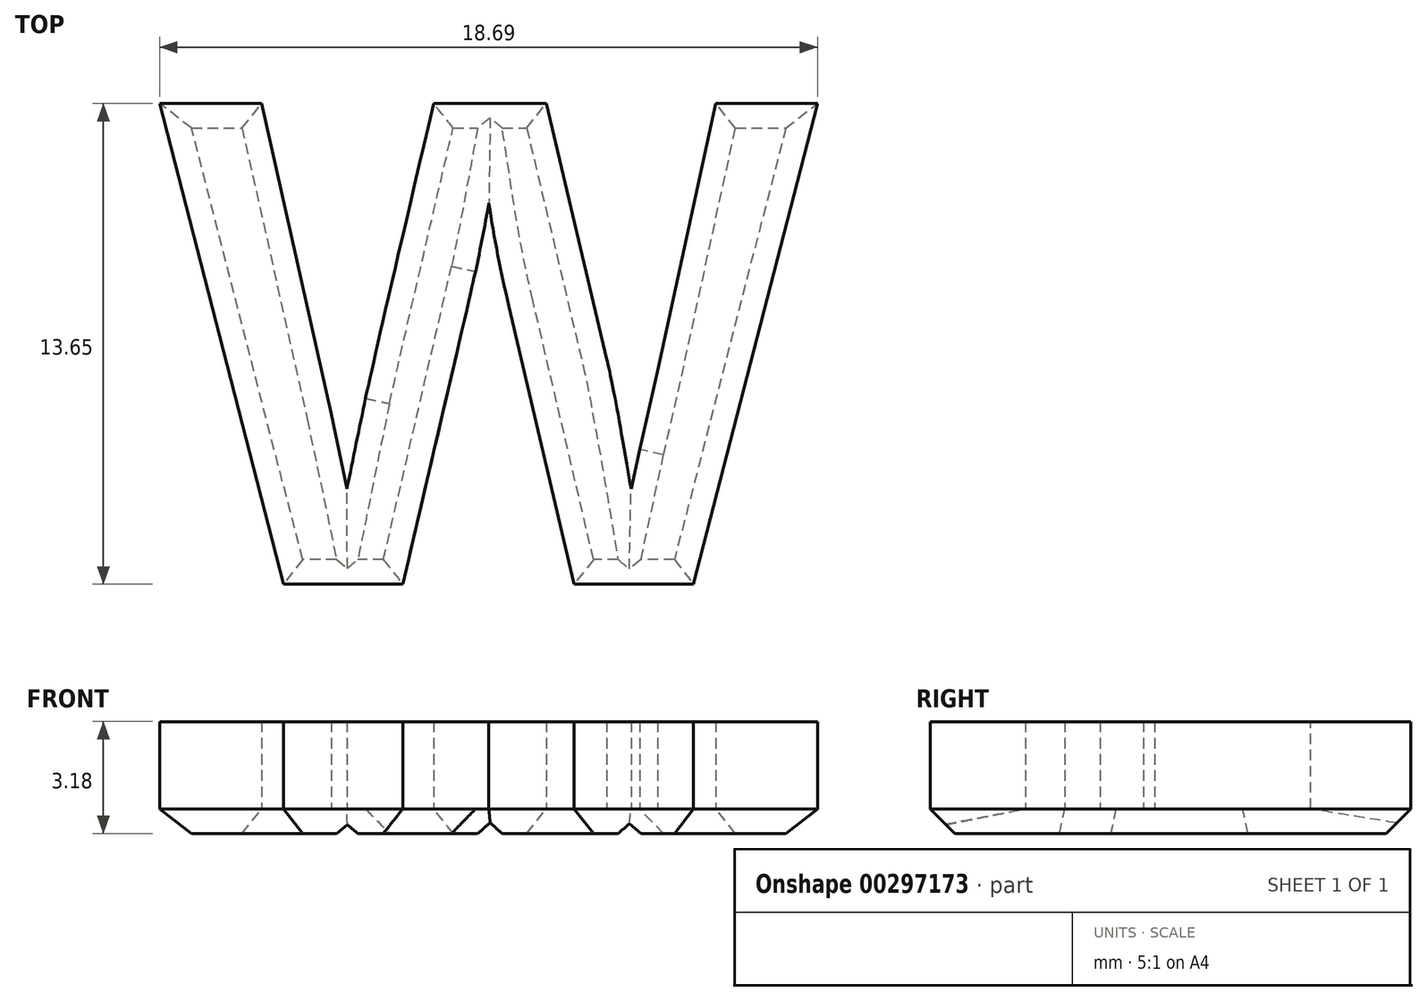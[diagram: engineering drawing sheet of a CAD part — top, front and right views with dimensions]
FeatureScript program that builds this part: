
annotation { "Feature Type Name" : "Feature", "Feature Type Description" : "" }
export const myFeature = defineFeature(function(context is Context, id is Id, definition is map)
    precondition{}
    {
        {
            var Q0;
            Q0=qCreatedBy(makeId("Top.planeOp"),FACE);
            var sketch = newSketch(context, id + "F0", { "sketchPlane" : qUnion([Q0])});
            skText(sketch, "E0", { "text": "W", "fontName": "Arimo-Bold.ttf"});
            const initialGuessF0  = {"E0": [0, -0.01429, 1, 0, 0.01429]};
            skSetInitialGuess(sketch, initialGuessF0);
            skSolve(sketch);
        }
        {
            var Q0;
            Q0=qSketchRegion(id+"F0",true);
            var Q1;
            Q1=qSketchRegion(id+"FFuAMvX4B0CXexs_0",true);
            var Q2;
            Q2=qSketchRegion(id+"F3e2CQsKu9PIjX0_0",true);
            var Q3;
            Q3=qSketchRegion(id+"F9LWrLlmn86MAX7_0",true);
            extrude(context, id + "F1", {"entities" : qUnion([Q0, Q1, Q2, Q3]), "depth" : 3.17 * mm});
        }
        {
            var Q0;
            Q0=makeQuery(id+"F1.opExtrude","CAP_FACE",FACE,{"disambiguationData":[OSD([sQuery(id+"F3e2CQsKu9PIjX0_0.wireOp",EDGE,"d36403c4-1396-490d-9497-49aafdbeb43d.sketch_text.stroke-0"),sQuery(id+"F3e2CQsKu9PIjX0_0.wireOp",EDGE,"d36403c4-1396-490d-9497-49aafdbeb43d.sketch_text.stroke-1"),sQuery(id+"F3e2CQsKu9PIjX0_0.wireOp",EDGE,"d36403c4-1396-490d-9497-49aafdbeb43d.sketch_text.stroke-2"),sQuery(id+"F3e2CQsKu9PIjX0_0.wireOp",EDGE,"d36403c4-1396-490d-9497-49aafdbeb43d.sketch_text.stroke-3"),sQuery(id+"F3e2CQsKu9PIjX0_0.wireOp",EDGE,"d36403c4-1396-490d-9497-49aafdbeb43d.sketch_text.stroke-4"),sQuery(id+"F3e2CQsKu9PIjX0_0.wireOp",EDGE,"d36403c4-1396-490d-9497-49aafdbeb43d.sketch_text.stroke-5"),sQuery(id+"F3e2CQsKu9PIjX0_0.wireOp",EDGE,"d36403c4-1396-490d-9497-49aafdbeb43d.sketch_text.stroke-6"),sQuery(id+"F3e2CQsKu9PIjX0_0.wireOp",EDGE,"d36403c4-1396-490d-9497-49aafdbeb43d.sketch_text.stroke-7"),sQuery(id+"F3e2CQsKu9PIjX0_0.wireOp",EDGE,"d36403c4-1396-490d-9497-49aafdbeb43d.sketch_text.stroke-8"),sQuery(id+"F3e2CQsKu9PIjX0_0.wireOp",EDGE,"d36403c4-1396-490d-9497-49aafdbeb43d.sketch_text.stroke-9"),sQuery(id+"F3e2CQsKu9PIjX0_0.wireOp",EDGE,"d36403c4-1396-490d-9497-49aafdbeb43d.sketch_text.stroke-10"),sQuery(id+"F3e2CQsKu9PIjX0_0.wireOp",EDGE,"d36403c4-1396-490d-9497-49aafdbeb43d.sketch_text.stroke-11"),sQuery(id+"F3e2CQsKu9PIjX0_0.wireOp",EDGE,"d36403c4-1396-490d-9497-49aafdbeb43d.sketch_text.stroke-12"),sQuery(id+"F3e2CQsKu9PIjX0_0.wireOp",EDGE,"d36403c4-1396-490d-9497-49aafdbeb43d.sketch_text.stroke-13"),sQuery(id+"F3e2CQsKu9PIjX0_0.wireOp",EDGE,"d36403c4-1396-490d-9497-49aafdbeb43d.sketch_text.stroke-14"),sQuery(id+"F3e2CQsKu9PIjX0_0.wireOp",EDGE,"d36403c4-1396-490d-9497-49aafdbeb43d.sketch_text.stroke-15"),sQuery(id+"F3e2CQsKu9PIjX0_0.wireOp",EDGE,"d36403c4-1396-490d-9497-49aafdbeb43d.sketch_text.stroke-16"),sQuery(id+"F3e2CQsKu9PIjX0_0.wireOp",EDGE,"d36403c4-1396-490d-9497-49aafdbeb43d.sketch_text.stroke-17"),sQuery(id+"F3e2CQsKu9PIjX0_0.wireOp",EDGE,"d36403c4-1396-490d-9497-49aafdbeb43d.sketch_text.stroke-18"),sQuery(id+"F3e2CQsKu9PIjX0_0.wireOp",EDGE,"d36403c4-1396-490d-9497-49aafdbeb43d.sketch_text.stroke-19"),sQuery(id+"F3e2CQsKu9PIjX0_0.wireOp",EDGE,"d36403c4-1396-490d-9497-49aafdbeb43d.sketch_text.stroke-20")])],"isStart":true});
            var Q1;
            Q1=makeQuery(id+"F1.opExtrude","CAP_FACE",FACE,{"disambiguationData":[OSD([sQuery(id+"FFuAMvX4B0CXexs_0.wireOp",EDGE,"ff5d8e69-f4ea-49cc-82ca-cbd897854416.sketch_text.stroke-0"),sQuery(id+"FFuAMvX4B0CXexs_0.wireOp",EDGE,"ff5d8e69-f4ea-49cc-82ca-cbd897854416.sketch_text.stroke-1"),sQuery(id+"FFuAMvX4B0CXexs_0.wireOp",EDGE,"ff5d8e69-f4ea-49cc-82ca-cbd897854416.sketch_text.stroke-2"),sQuery(id+"FFuAMvX4B0CXexs_0.wireOp",EDGE,"ff5d8e69-f4ea-49cc-82ca-cbd897854416.sketch_text.stroke-3"),sQuery(id+"FFuAMvX4B0CXexs_0.wireOp",EDGE,"ff5d8e69-f4ea-49cc-82ca-cbd897854416.sketch_text.stroke-4"),sQuery(id+"FFuAMvX4B0CXexs_0.wireOp",EDGE,"ff5d8e69-f4ea-49cc-82ca-cbd897854416.sketch_text.stroke-5"),sQuery(id+"FFuAMvX4B0CXexs_0.wireOp",EDGE,"ff5d8e69-f4ea-49cc-82ca-cbd897854416.sketch_text.stroke-6"),sQuery(id+"FFuAMvX4B0CXexs_0.wireOp",EDGE,"ff5d8e69-f4ea-49cc-82ca-cbd897854416.sketch_text.stroke-7"),sQuery(id+"FFuAMvX4B0CXexs_0.wireOp",EDGE,"ff5d8e69-f4ea-49cc-82ca-cbd897854416.sketch_text.stroke-8"),sQuery(id+"FFuAMvX4B0CXexs_0.wireOp",EDGE,"ff5d8e69-f4ea-49cc-82ca-cbd897854416.sketch_text.stroke-9"),sQuery(id+"FFuAMvX4B0CXexs_0.wireOp",EDGE,"ff5d8e69-f4ea-49cc-82ca-cbd897854416.sketch_text.stroke-10"),sQuery(id+"FFuAMvX4B0CXexs_0.wireOp",EDGE,"ff5d8e69-f4ea-49cc-82ca-cbd897854416.sketch_text.stroke-11"),sQuery(id+"FFuAMvX4B0CXexs_0.wireOp",EDGE,"ff5d8e69-f4ea-49cc-82ca-cbd897854416.sketch_text.stroke-12"),sQuery(id+"FFuAMvX4B0CXexs_0.wireOp",EDGE,"ff5d8e69-f4ea-49cc-82ca-cbd897854416.sketch_text.stroke-13"),sQuery(id+"FFuAMvX4B0CXexs_0.wireOp",EDGE,"ff5d8e69-f4ea-49cc-82ca-cbd897854416.sketch_text.stroke-14"),sQuery(id+"FFuAMvX4B0CXexs_0.wireOp",EDGE,"ff5d8e69-f4ea-49cc-82ca-cbd897854416.sketch_text.stroke-15"),sQuery(id+"FFuAMvX4B0CXexs_0.wireOp",EDGE,"ff5d8e69-f4ea-49cc-82ca-cbd897854416.sketch_text.stroke-16")])],"isStart":true});
            var Q2;
            Q2=makeQuery(id+"F1.opExtrude","CAP_FACE",FACE,{"disambiguationData":[OSD([sQuery(id+"F9LWrLlmn86MAX7_0.wireOp",EDGE,"c90eff37-dab6-43ec-bed2-d4ad99606f9c.sketch_text.stroke-0"),sQuery(id+"F9LWrLlmn86MAX7_0.wireOp",EDGE,"c90eff37-dab6-43ec-bed2-d4ad99606f9c.sketch_text.stroke-1"),sQuery(id+"F9LWrLlmn86MAX7_0.wireOp",EDGE,"c90eff37-dab6-43ec-bed2-d4ad99606f9c.sketch_text.stroke-2"),sQuery(id+"F9LWrLlmn86MAX7_0.wireOp",EDGE,"c90eff37-dab6-43ec-bed2-d4ad99606f9c.sketch_text.stroke-3"),sQuery(id+"F9LWrLlmn86MAX7_0.wireOp",EDGE,"c90eff37-dab6-43ec-bed2-d4ad99606f9c.sketch_text.stroke-4"),sQuery(id+"F9LWrLlmn86MAX7_0.wireOp",EDGE,"c90eff37-dab6-43ec-bed2-d4ad99606f9c.sketch_text.stroke-5"),sQuery(id+"F9LWrLlmn86MAX7_0.wireOp",EDGE,"c90eff37-dab6-43ec-bed2-d4ad99606f9c.sketch_text.stroke-6"),sQuery(id+"F9LWrLlmn86MAX7_0.wireOp",EDGE,"c90eff37-dab6-43ec-bed2-d4ad99606f9c.sketch_text.stroke-7"),sQuery(id+"F9LWrLlmn86MAX7_0.wireOp",EDGE,"c90eff37-dab6-43ec-bed2-d4ad99606f9c.sketch_text.stroke-8"),sQuery(id+"F9LWrLlmn86MAX7_0.wireOp",EDGE,"c90eff37-dab6-43ec-bed2-d4ad99606f9c.sketch_text.stroke-9"),sQuery(id+"F9LWrLlmn86MAX7_0.wireOp",EDGE,"c90eff37-dab6-43ec-bed2-d4ad99606f9c.sketch_text.stroke-10"),sQuery(id+"F9LWrLlmn86MAX7_0.wireOp",EDGE,"c90eff37-dab6-43ec-bed2-d4ad99606f9c.sketch_text.stroke-11"),sQuery(id+"F9LWrLlmn86MAX7_0.wireOp",EDGE,"c90eff37-dab6-43ec-bed2-d4ad99606f9c.sketch_text.stroke-12"),sQuery(id+"F9LWrLlmn86MAX7_0.wireOp",EDGE,"c90eff37-dab6-43ec-bed2-d4ad99606f9c.sketch_text.stroke-13"),sQuery(id+"F9LWrLlmn86MAX7_0.wireOp",EDGE,"c90eff37-dab6-43ec-bed2-d4ad99606f9c.sketch_text.stroke-14"),sQuery(id+"F9LWrLlmn86MAX7_0.wireOp",EDGE,"c90eff37-dab6-43ec-bed2-d4ad99606f9c.sketch_text.stroke-15"),sQuery(id+"F9LWrLlmn86MAX7_0.wireOp",EDGE,"c90eff37-dab6-43ec-bed2-d4ad99606f9c.sketch_text.stroke-16")])],"isStart":true});
            var Q3;
            Q3=makeQuery(id+"F1.opExtrude","CAP_FACE",FACE,{"disambiguationData":[OSD([sQuery(id+"F0.wireOp",EDGE,"E0.sketch_text.stroke-0"),sQuery(id+"F0.wireOp",EDGE,"E0.sketch_text.stroke-1"),sQuery(id+"F0.wireOp",EDGE,"E0.sketch_text.stroke-2"),sQuery(id+"F0.wireOp",EDGE,"E0.sketch_text.stroke-3"),sQuery(id+"F0.wireOp",EDGE,"E0.sketch_text.stroke-4"),sQuery(id+"F0.wireOp",EDGE,"E0.sketch_text.stroke-5"),sQuery(id+"F0.wireOp",EDGE,"E0.sketch_text.stroke-6"),sQuery(id+"F0.wireOp",EDGE,"E0.sketch_text.stroke-7"),sQuery(id+"F0.wireOp",EDGE,"E0.sketch_text.stroke-8"),sQuery(id+"F0.wireOp",EDGE,"E0.sketch_text.stroke-9"),sQuery(id+"F0.wireOp",EDGE,"E0.sketch_text.stroke-10"),sQuery(id+"F0.wireOp",EDGE,"E0.sketch_text.stroke-11"),sQuery(id+"F0.wireOp",EDGE,"E0.sketch_text.stroke-12"),sQuery(id+"F0.wireOp",EDGE,"E0.sketch_text.stroke-13"),sQuery(id+"F0.wireOp",EDGE,"E0.sketch_text.stroke-14"),sQuery(id+"F0.wireOp",EDGE,"E0.sketch_text.stroke-15"),sQuery(id+"F0.wireOp",EDGE,"E0.sketch_text.stroke-16"),sQuery(id+"F0.wireOp",EDGE,"E0.sketch_text.stroke-17"),sQuery(id+"F0.wireOp",EDGE,"E0.sketch_text.stroke-18"),sQuery(id+"F0.wireOp",EDGE,"E0.sketch_text.stroke-19"),sQuery(id+"F0.wireOp",EDGE,"VDZtHXXc-oGIx-YDzq-gdON-jcRySN0DwnXJ"),sQuery(id+"F0.wireOp",EDGE,"QN5iSeOg-hT6p-hmbR-ICrl-aOOzazcwX9CO")])],"isStart":true});
            chamfer(context, id + "F2", {"entities" : qUnion([Q0, Q1, Q2, Q3]), "width" : 0.7 * mm, "tangentPropagation" : true});
        }
    });
